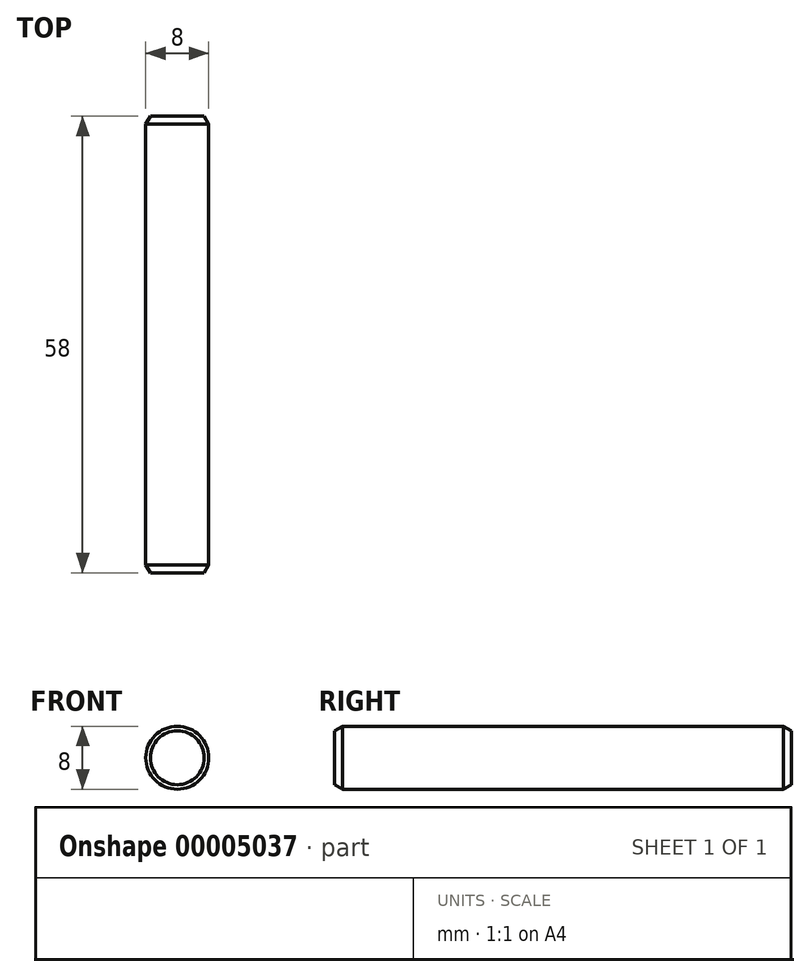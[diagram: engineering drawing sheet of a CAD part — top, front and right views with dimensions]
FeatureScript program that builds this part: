
annotation { "Feature Type Name" : "Feature", "Feature Type Description" : "" }
export const myFeature = defineFeature(function(context is Context, id is Id, definition is map)
    precondition{}
    {
        {
            var Q0;
            Q0=qCreatedBy(makeId("Front.planeOp"),FACE);
            var sketch = newSketch(context, id + "F0", { "sketchPlane" : qUnion([Q0])});
            skCircle(sketch, "E0", {"center": v(0, 0) * mm, "radius": 4 * mm});
            skSolve(sketch);
        }
        {
            var Q0;
            Q0 = qSketchRegion(id + "F0", true);
            extrude(context, id + "F1", {"entities" : qUnion([Q0]), "depth" : 58 * mm});
        }
        {
            var Q0;
            Q0=makeQuery(id+"F1.opExtrude","CAP_EDGE",EDGE,{"disambiguationData":[OSD([sQuery(id+"F0.wireOp",EDGE,"E0")])],"isStart":true});
            var Q1;
            Q1=makeQuery(id+"F1.opExtrude","CAP_EDGE",EDGE,{"disambiguationData":[OSD([sQuery(id+"F0.wireOp",EDGE,"E0")])],"isStart":false});
            chamfer(context, id + "F2", {"entities" : qUnion([Q0, Q1]), "chamferType" : ChamferType.OFFSET_ANGLE, "width" : 1 * mm, "oppositeDirection" : false, "angle" : 30 * degree, "tangentPropagation" : true});
        }
    });
